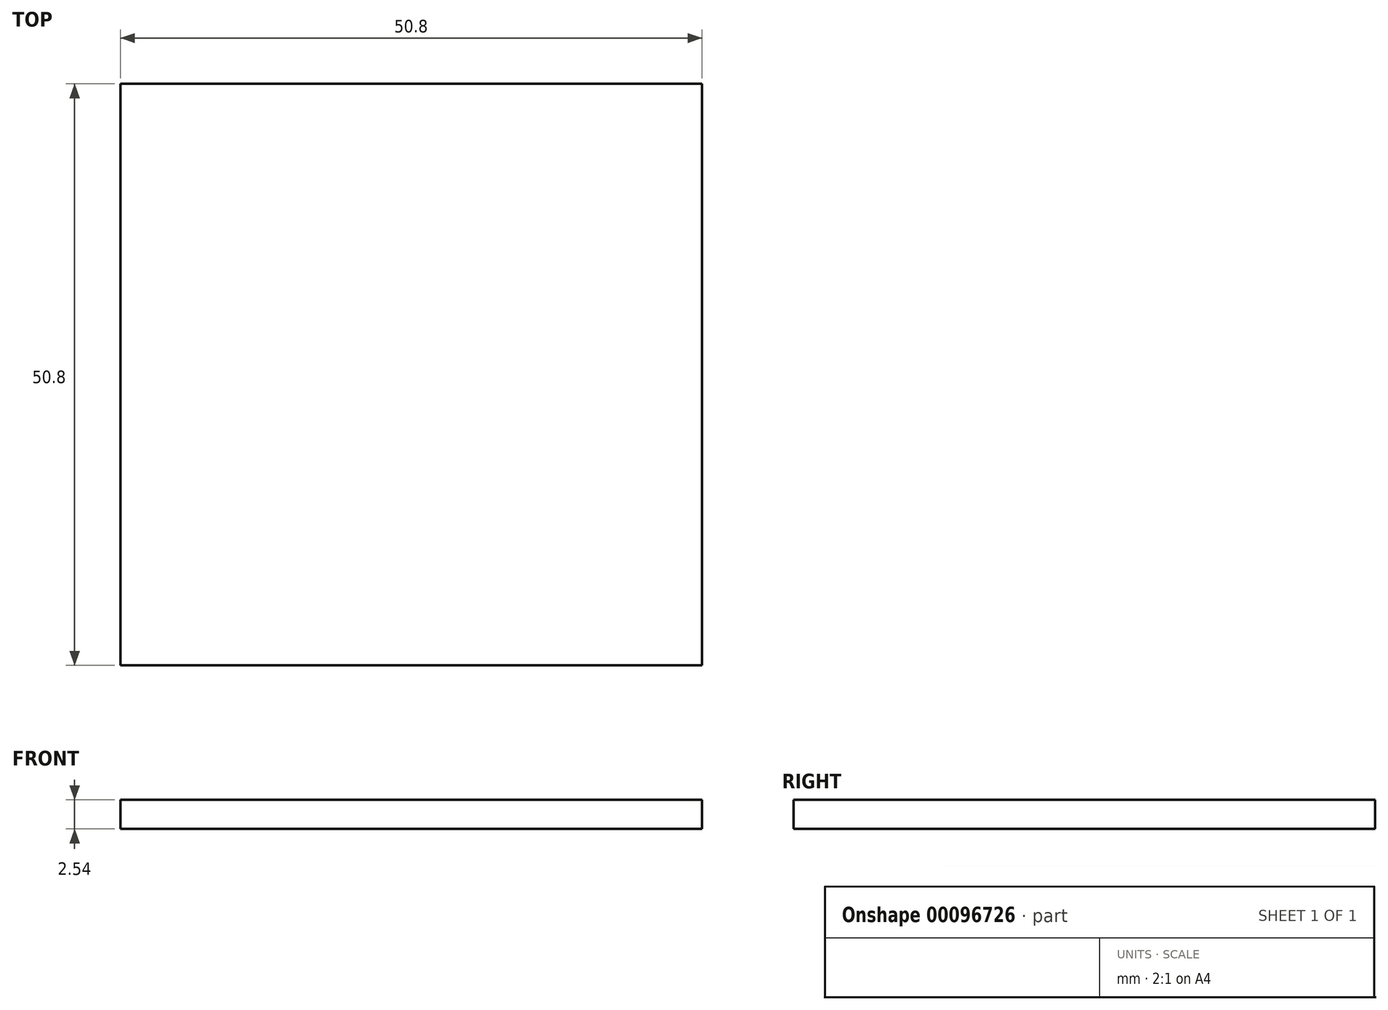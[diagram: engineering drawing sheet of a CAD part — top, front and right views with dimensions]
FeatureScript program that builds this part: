
annotation { "Feature Type Name" : "Feature", "Feature Type Description" : "" }
export const myFeature = defineFeature(function(context is Context, id is Id, definition is map)
    precondition{}
    {
        {
            var Q0;
            Q0=qCreatedBy(makeId("Top.planeOp"),FACE);
            var sketch = newSketch(context, id + "F0", { "sketchPlane" : qUnion([Q0])});
            skLineSegment(sketch, "E0.bottom", {"start": v(-28.02, 34.93) * mm, "end": v(22.78, 34.93) * mm});
            skLineSegment(sketch, "E0.top", {"start": v(-28.02, -15.87) * mm, "end": v(22.78, -15.87) * mm});
            skLineSegment(sketch, "E0.left", {"start": v(-28.02, 34.93) * mm, "end": v(-28.02, -15.87) * mm});
            skLineSegment(sketch, "E0.right", {"start": v(22.78, 34.93) * mm, "end": v(22.78, -15.87) * mm});
            skSolve(sketch);
        }
        {
            var Q0;
            Q0 = qSketchRegion(id + "F0", true);
            extrude(context, id + "F1", {"entities" : qUnion([Q0]), "depth" : 2.54 * mm});
        }
    });
